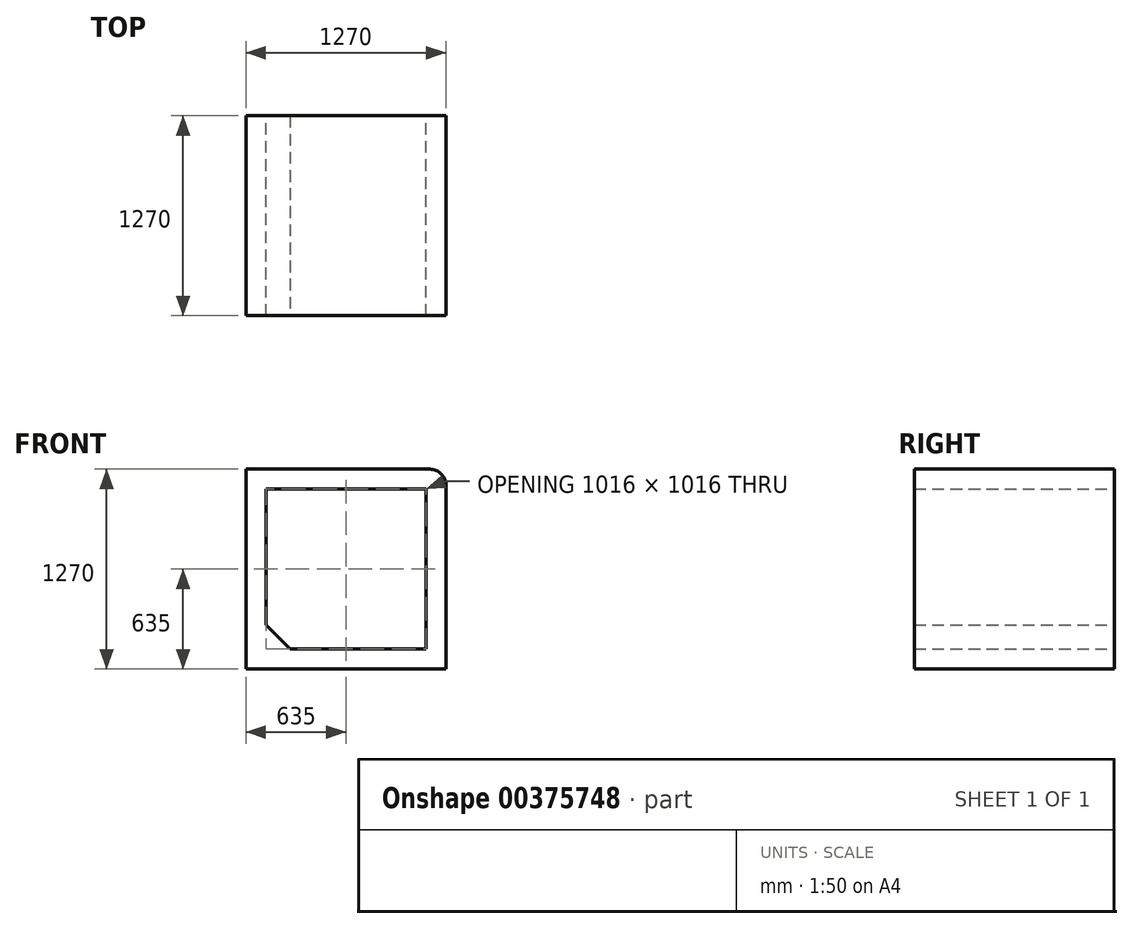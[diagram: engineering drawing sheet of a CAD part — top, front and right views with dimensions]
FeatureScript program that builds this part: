
annotation { "Feature Type Name" : "Feature", "Feature Type Description" : "" }
export const myFeature = defineFeature(function(context is Context, id is Id, definition is map)
    precondition{}
    {
        {
            var Q0;
            Q0=qCreatedBy(makeId("Front.planeOp"),FACE);
            var sketch = newSketch(context, id + "F0", { "sketchPlane" : qUnion([Q0])});
            skLineSegment(sketch, "E0.bottom", {"start": v(508, 508) * mm, "end": v(-508, 508) * mm});
            skLineSegment(sketch, "E0.top", {"start": v(508, -508) * mm, "end": v(-508, -508) * mm});
            skLineSegment(sketch, "E0.left", {"start": v(508, 508) * mm, "end": v(508, -508) * mm});
            skLineSegment(sketch, "E0.right", {"start": v(-508, 508) * mm, "end": v(-508, -508) * mm});
            skPoint(sketch, "E0.middle", {"position": v(0, 0) * mm});
            skLineSegment(sketch, "E1.bottom", {"start": v(635, -635) * mm, "end": v(-635, -635) * mm});
            skLineSegment(sketch, "E1.top", {"start": v(635, 635) * mm, "end": v(-635, 635) * mm});
            skLineSegment(sketch, "E1.left", {"start": v(635, -635) * mm, "end": v(635, 635) * mm});
            skLineSegment(sketch, "E1.right", {"start": v(-635, -635) * mm, "end": v(-635, 635) * mm});
            skSolve(sketch);
        }
        {
            var Q0;
            Q0=makeQuery(id+"F0.imprint","IMPRINT",FACE,{"disambiguationData":[TD([[makeQuery(id+"F0.imprint","IMPRINT",EDGE,{"derivedFrom":sQuery(id+"F0.wireOp",EDGE,"E0.bottom")}),-1.0]])]});
            extrude(context, id + "F1", {"entities" : qUnion([Q0]), "endBound" : BoundingType.SYMMETRIC, "depth" : 1270 * mm});
        }
        {
            var Q0;
            Q0=makeQuery(id+"F1.opExtrude","SWEPT_EDGE",EDGE,{"disambiguationData":[OSD([sQuery(id+"F0.wireOp",EDGE,"E1.top"),sQuery(id+"F0.wireOp",EDGE,"E1.left")])]});
            fillet(context, id + "F2", {"entities" : qUnion([Q0]), "radius" : 101.6 * mm, "tangentPropagation" : true, "allowEdgeOverflow" : false});
        }
        {
            var Q0;
            Q0=makeQuery(id+"F1.opExtrude","SWEPT_EDGE",EDGE,{"disambiguationData":[OSD([sQuery(id+"F0.wireOp",EDGE,"E0.top"),sQuery(id+"F0.wireOp",EDGE,"E0.right")])]});
            chamfer(context, id + "F3", {"entities" : qUnion([Q0]), "width" : 152.4 * mm, "tangentPropagation" : true});
        }
    });
